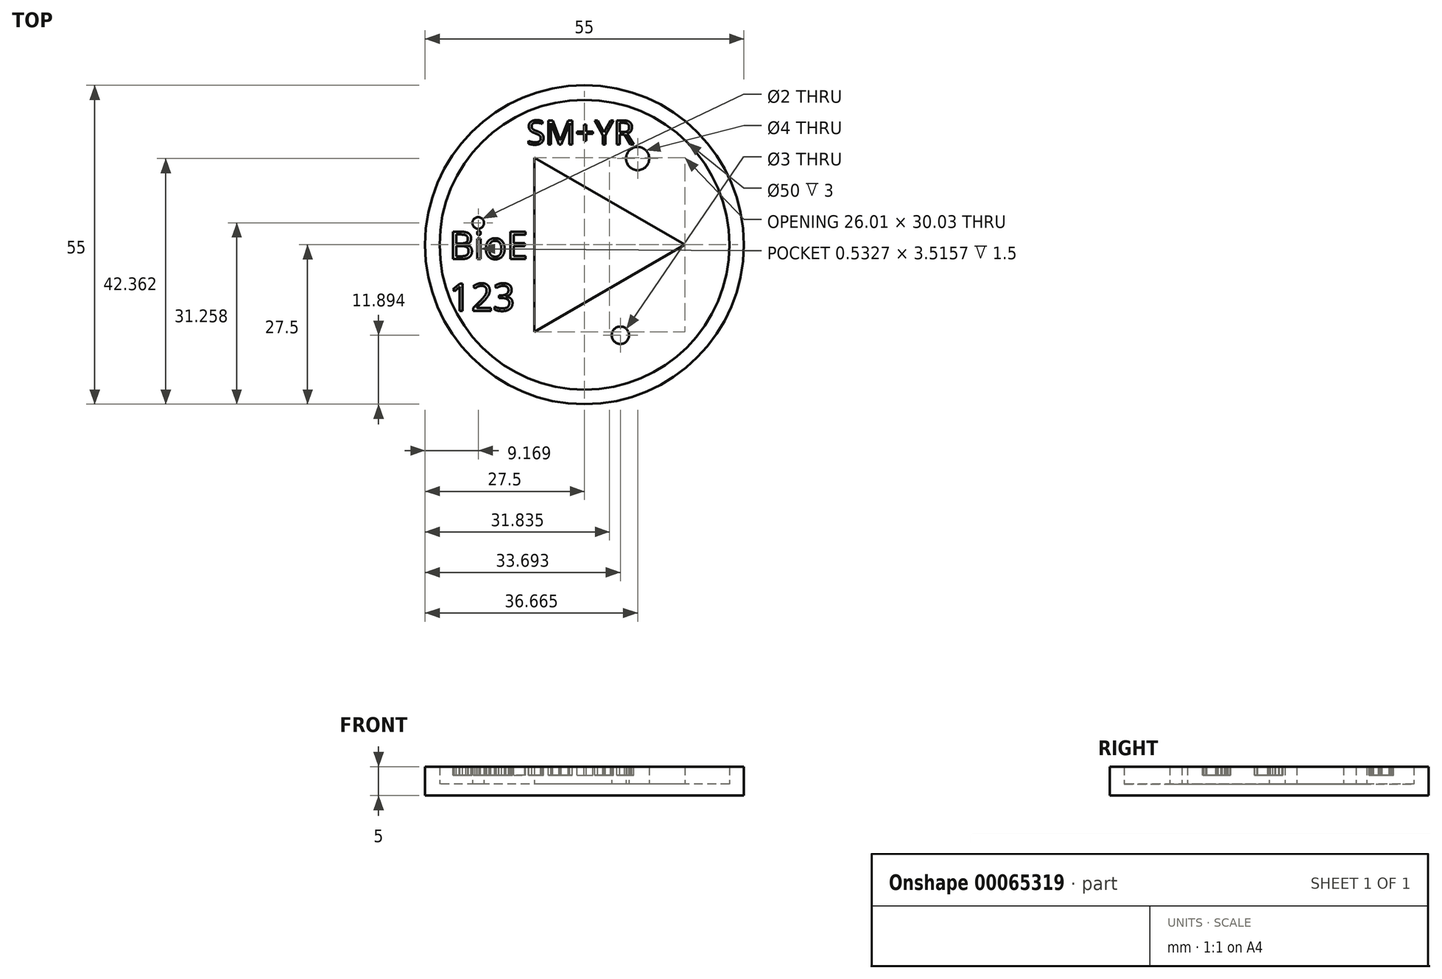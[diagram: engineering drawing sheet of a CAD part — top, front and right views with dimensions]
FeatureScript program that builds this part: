
annotation { "Feature Type Name" : "Feature", "Feature Type Description" : "" }
export const myFeature = defineFeature(function(context is Context, id is Id, definition is map)
    precondition{}
    {
        {
            var Q0;
            Q0=qCreatedBy(makeId("Top.planeOp"),FACE);
            var sketch = newSketch(context, id + "F0", { "sketchPlane" : qUnion([Q0])});
            skCircle(sketch, "E0", {"center": v(0, 0) * mm, "radius": 27.5 * mm});
            skSolve(sketch);
        }
        {
            var Q0;
            Q0=makeQuery(id+"F0.imprint","IMPRINT",FACE,{"disambiguationData":[TD([[makeQuery(id+"F0.imprint","IMPRINT",EDGE,{"derivedFrom":sQuery(id+"F0.wireOp",EDGE,"E0")}),1.0]])]});
            extrude(context, id + "F1", {"entities" : qUnion([Q0]), "depth" : 5 * mm});
        }
        {
            var Q0;
            Q0=makeQuery(id+"F1.opExtrude","CAP_FACE",FACE,{"disambiguationData":[OSD([sQuery(id+"F0.wireOp",EDGE,"E0")])],"isStart":false});
            var sketch = newSketch(context, id + "F2", { "sketchPlane" : qUnion([Q0])});
            skCircle(sketch, "E1", {"center": v(0, 0) * mm, "radius": 25 * mm});
            skCircle(sketch, "E2.cCircle", {"center": v(0, 0) * mm, "radius": 8.67 * mm, "construction": true});
            skLineSegment(sketch, "E2.0", {"start": v(-8.67, -15.02) * mm, "end": v(-8.67, 15.02) * mm});
            skLineSegment(sketch, "E2.1", {"start": v(-8.67, 15.02) * mm, "end": v(17.34, 0) * mm});
            skLineSegment(sketch, "E2.2", {"start": v(17.34, 0) * mm, "end": v(-8.67, -15.02) * mm});
            skPoint(sketch, "E2.0.midPoint", {"position": v(-8.67, 0) * mm});
            skCircle(sketch, "E3", {"center": v(-18.33, 3.76) * mm, "radius": 1 * mm});
            skCircle(sketch, "E4", {"center": v(9.17, 14.86) * mm, "radius": 2 * mm});
            skCircle(sketch, "E5", {"center": v(6.2, -15.6) * mm, "radius": 1.5 * mm});
            skSolve(sketch);
        }
        {
            var Q0;
            Q0=makeQuery(id+"F2.imprint","IMPRINT",FACE,{"disambiguationData":[TD([[makeQuery(id+"F2.imprint","IMPRINT",EDGE,{"derivedFrom":sQuery(id+"F2.wireOp",EDGE,"E1")}),1.0]])]});
            extrude(context, id + "F3", {"entities" : qUnion([Q0]), "operationType" : NewBodyOperationType.REMOVE, "oppositeDirection" : true, "depth" : 3 * mm});
        }
        {
            var Q0;
            Q0=makeQuery(id+"F2.imprint","IMPRINT",FACE,{"disambiguationData":[TD([[makeQuery(id+"F2.imprint","IMPRINT",EDGE,{"derivedFrom":sQuery(id+"F2.wireOp",EDGE,"E2.0")}),-1.0]])]});
            extrude(context, id + "F4", {"entities" : qUnion([Q0]), "operationType" : NewBodyOperationType.ADD, "oppositeDirection" : true, "depth" : 3 * mm});
        }
        {
            var Q0;
            Q0=makeQuery(id+"F3.boolean.opBoolean","COPY",FACE,{"derivedFrom":makeQuery(id+"F3.opExtrude","CAP_FACE",FACE,{"disambiguationData":[OSD([sQuery(id+"F2.wireOp",EDGE,"E1"),sQuery(id+"F2.wireOp",EDGE,"E2.0"),sQuery(id+"F2.wireOp",EDGE,"E2.1"),sQuery(id+"F2.wireOp",EDGE,"E2.2"),sQuery(id+"F2.wireOp",EDGE,"E3"),sQuery(id+"F2.wireOp",EDGE,"E4"),sQuery(id+"F2.wireOp",EDGE,"E5")])],"isStart":false})});
            extrude(context, id + "F5", {"entities" : qUnion([Q0]), "depth" : 3 * mm});
        }
        {
            var Q0;
            Q0=makeQuery(id+"F5.opExtrude","CAP_FACE",FACE,{"disambiguationData":[OSD([sQuery(id+"F2.wireOp",EDGE,"E1"),sQuery(id+"F2.wireOp",EDGE,"E2.0"),sQuery(id+"F2.wireOp",EDGE,"E2.1"),sQuery(id+"F2.wireOp",EDGE,"E2.2"),sQuery(id+"F2.wireOp",EDGE,"E3"),sQuery(id+"F2.wireOp",EDGE,"E4"),sQuery(id+"F2.wireOp",EDGE,"E5")])],"isStart":false});
            var sketch = newSketch(context, id + "F6", { "sketchPlane" : qUnion([Q0])});
            skText(sketch, "E6", { "text": "SM+YR\n", "fontName": "OpenSans-Regular.ttf"});
            skText(sketch, "E7", { "text": "BioE\n123\n", "fontName": "OpenSans-Regular.ttf"});
            const initialGuessF6  = {"E6": [-0.00996, 0.0173, 1, 0, 0.00417], "E7": [-0.0233, -0.00245, 1, 0, 0.00473]};
            skSetInitialGuess(sketch, initialGuessF6);
            skSolve(sketch);
        }
        {
            var Q0;
            Q0 = qSketchRegion(id + "F6", true);
            extrude(context, id + "F7", {"entities" : qUnion([Q0]), "operationType" : NewBodyOperationType.REMOVE, "oppositeDirection" : true, "depth" : 1 * mm});
        }
        {
            var Q0;
            Q0 = qSketchRegion(id + "F6", true);
            extrude(context, id + "F8", {"entities" : qUnion([Q0]), "operationType" : NewBodyOperationType.REMOVE, "oppositeDirection" : true, "depth" : 1.5 * mm});
        }
    });
